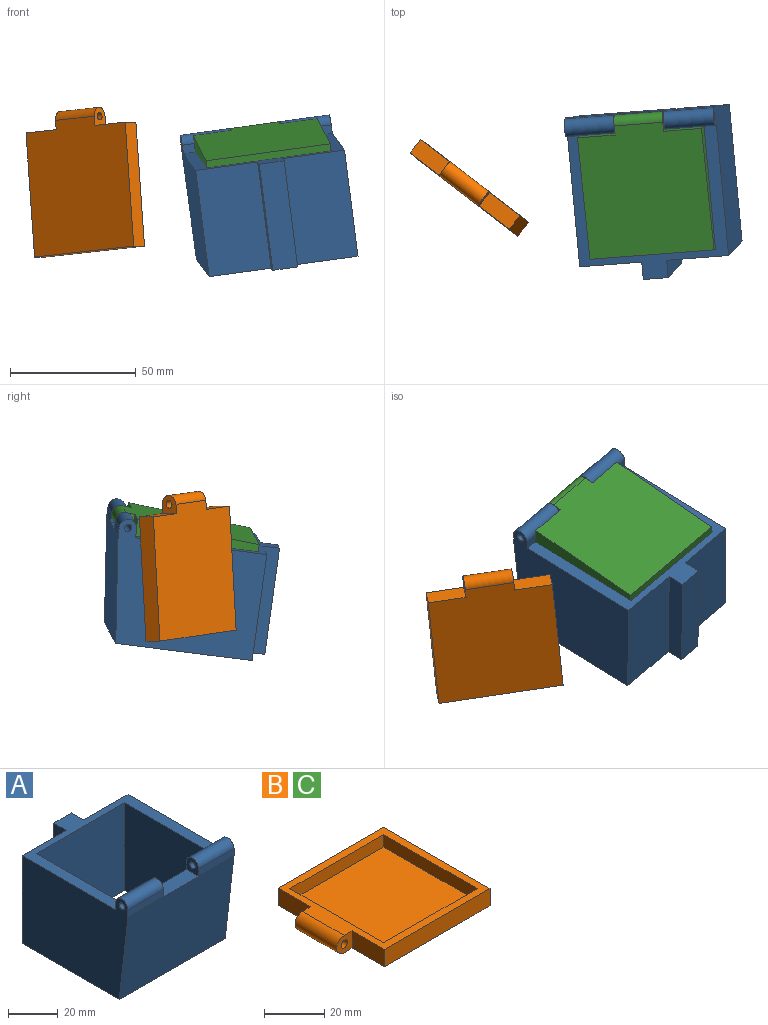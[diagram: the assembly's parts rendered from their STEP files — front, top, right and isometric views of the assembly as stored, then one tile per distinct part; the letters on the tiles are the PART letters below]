
ASSEMBLY  parts=3 mates=1
PART A: 23 faces, bbox 60x67x50 mm
  f0: plane 43x25mm, normal (0,1,0), area 1075mm2, adj f2,f7,f20,f21
  f1: plane 43x25mm, normal (0,1,0), area 1075mm2, adj f5,f7,f20,f22
  f2: plane 60x50mm, normal (-1,0,0), area 2509.2mm2, adj f0,f7,f11,f13,f14,f15,f16,f20
  f3: plane 50x43mm, normal (0,-1,0), area 2150mm2, adj f4,f6,f7,f20
  f4: plane 50x43mm, normal (1,0,0), area 2150mm2, adj f3,f7,f13,f20
  f5: plane 60x50mm, normal (1,0,0), area 2509.2mm2, adj f1,f7,f8,f9,f10,f11,f13,f20
  f6: plane 50x43mm, normal (-1,0,0), area 2150mm2, adj f3,f7,f13,f20
  f7: plane 62x60mm, normal (0,0,-1), area 870mm2, adj f0,f1,f2,f3,f4,f5,f6,f11
  f8: plane 20x3.5mm, normal (0,-1,0), area 70mm2, adj f5,f9,f11,f18
  f9: cylinder r=3.5mm len=20mm, axis (-1,0,0), area 219.9mm2, adj f5,f8,f13,f18
  f10: cylinder r=1.5mm len=20mm, axis (1,0,0), area 188.5mm2, adj f5,f18
  f11: plane 60x43mm, normal (0,-0.99,-0.12), area 2593.4mm2, adj f2,f5,f7,f8,f14,f17,f18,f19
  f12: plane 43x10mm, normal (0,1,0), area 430mm2, adj f7,f20,f21,f22
  f13: plane 60x46.5mm, normal (0,1,0), area 2286mm2, adj f2,f4,f5,f6,f7,f9,f15,f17
  f14: plane 20x3.5mm, normal (0,-1,0), area 70mm2, adj f2,f11,f15,f17
  f15: cylinder r=3.5mm len=20mm, axis (-1,0,0), area 219.9mm2, adj f2,f13,f14,f17
  f16: cylinder r=1.5mm len=20mm, axis (1,0,0), area 188.5mm2, adj f2,f17
  f17: plane 7.2x7mm, normal (1,0,0), area 38.1mm2, adj f11,f13,f14,f15,f16,f19
  f18: plane 7.2x7mm, normal (-1,0,0), area 38.1mm2, adj f8,f9,f10,f11,f13,f19
  f19: plane 20x6.98mm, normal (0,0,1), area 139.5mm2, adj f11,f13,f17,f18
  f20: plane 60x60mm, normal (0,0,1), area 750mm2, adj f0,f1,f2,f3,f4,f5,f6,f12
  f21: plane 43x7mm, normal (-1,0,0), area 301mm2, adj f0,f7,f12,f20
  f22: plane 43x7mm, normal (1,0,0), area 301mm2, adj f1,f7,f12,f20
PART B: 16 faces, bbox 56.8x50x7 mm
  f0: plane 15.2x7mm, normal (-1,0,0), area 106.4mm2, adj f1,f6,f7,f8
  f1: plane 49.6x7mm, normal (0,-1,0), area 347.2mm2, adj f0,f2,f7,f8
  f2: plane 50x7mm, normal (1,0,0), area 350mm2, adj f1,f3,f7,f8
  f3: plane 49.6x7mm, normal (0,1,0), area 347.2mm2, adj f2,f4,f7,f8
  f4: plane 15.2x7mm, normal (-1,0,0), area 106.4mm2, adj f3,f5,f7,f8
  f5: plane 7.2x7mm, normal (0,1,0), area 38.1mm2, adj f4,f7,f8,f9,f10
  f6: plane 7.2x7mm, normal (0,-1,0), area 38.1mm2, adj f0,f7,f8,f9,f10
  f7: plane 53.3x50mm, normal (0,0,1), area 616.5mm2, adj f0,f1,f2,f3,f4,f5,f6,f9
  f8: plane 53.3x50mm, normal (0,0,-1), area 2552.5mm2, adj f0,f1,f2,f3,f4,f5,f6,f9
  f9: cylinder r=3.5mm len=19.6mm, axis (0,1,0), area 215.5mm2, adj f5,f6,f7,f8
  f10: cylinder r=1.5mm len=19.6mm, axis (0,1,0), area 184.7mm2, adj f5,f6
  f11: plane 44x5mm, normal (1,0,0), area 220mm2, adj f7,f12,f14,f15
  f12: plane 44x5mm, normal (0,1,0), area 220mm2, adj f7,f11,f13,f15
  f13: plane 44x5mm, normal (-1,0,0), area 220mm2, adj f7,f12,f14,f15
  f14: plane 44x5mm, normal (0,-1,0), area 220mm2, adj f7,f11,f13,f15
  f15: plane 44x44mm, normal (0,0,1), area 1936mm2, adj f11,f12,f13,f14
PART C: same geometry as B
PLACE A rot(axis=(0.07,0.07,-1),175.2deg) t=(101.09,121.15,-21.45)mm
PLACE B rot(axis=(-0.45,0.81,0.37),99.3deg) t=(49.46,116.35,12.96)mm
PLACE C rot(axis=(-0.74,0.67,0.03),166.4deg) t=(121.76,119.97,29.93)mm
MATE revolute C.f9 <-> A.f9  axis (-0.99,-0.07,-0.14) through (109.97,144.25,30.21)mm
